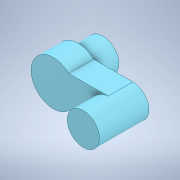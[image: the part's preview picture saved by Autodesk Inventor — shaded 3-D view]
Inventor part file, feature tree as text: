
AUTODESK INVENTOR PART (.ipt)
format: ipt  version: 2022 (Build 260153000, 153)  size: 131,584 bytes
history: native  units: in
note: dims shown in document units (in); Inventor stores cm internally (conversion verified against a paired STEP export)
features: extrude x3, sketch x2
ambient origin geometry x8: Origin, YZ Plane, XZ Plane, XY Plane, X Axis, Y Axis, Z Axis, Center Point
bodies: Solid1 (feature_tree)
feature tree (5):
  sketch  "Sketch2"  dims[d0=0.1969in d1=0.0in d2=0.1969in d3=0.0in]
  extrude  "Extrusion1"  Depth=0.1969in TaperAngle=0.0deg
  extrude  "Extrusion2"  Depth=0.2559in
  extrude  "Extrusion3"  Depth=0.2559in
  sketch  "Sketch3"  dims[d4=0.1969in d5=0.0in d6=0.4354in d7=0.2559in d8=0.2559in d9=0.3543in]
